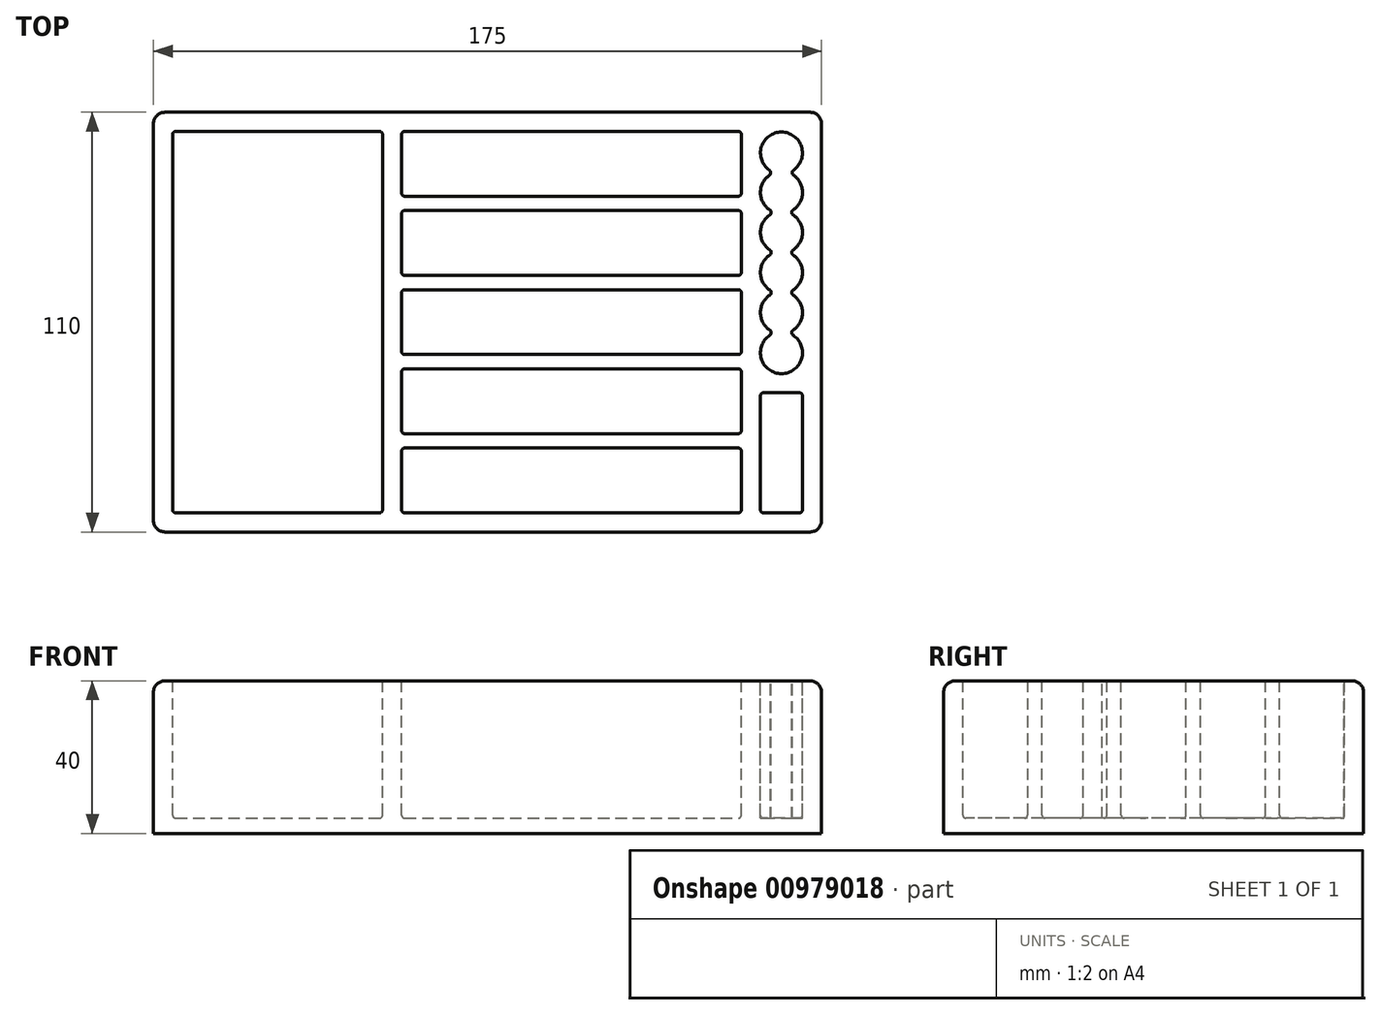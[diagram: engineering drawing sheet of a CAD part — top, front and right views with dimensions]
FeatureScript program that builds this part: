
annotation { "Feature Type Name" : "Feature", "Feature Type Description" : "" }
export const myFeature = defineFeature(function(context is Context, id is Id, definition is map)
    precondition{}
    {
        {
            var Q0;
            Q0=qCreatedBy(makeId("Top.planeOp"),FACE);
            var sketch = newSketch(context, id + "F0", { "sketchPlane" : qUnion([Q0])});
            skLineSegment(sketch, "E0.bottom", {"start": v(87.5, 55) * mm, "end": v(-87.5, 55) * mm});
            skLineSegment(sketch, "E0.top", {"start": v(87.5, -55) * mm, "end": v(-87.5, -55) * mm});
            skLineSegment(sketch, "E0.left", {"start": v(87.5, 55) * mm, "end": v(87.5, -55) * mm});
            skLineSegment(sketch, "E0.right", {"start": v(-87.5, 55) * mm, "end": v(-87.5, -55) * mm});
            skPoint(sketch, "E0.middle", {"position": v(0, 0) * mm});
            skSolve(sketch);
        }
        {
            var Q0;
            Q0=makeQuery(id+"F0.imprint","IMPRINT",FACE,{"disambiguationData":[TD([[makeQuery(id+"F0.imprint","IMPRINT",EDGE,{"derivedFrom":sQuery(id+"F0.wireOp",EDGE,"E0.bottom")}),1.0]])]});
            extrude(context, id + "F1", {"entities" : qUnion([Q0]), "depth" : 40 * mm, "offsetDistance" : 25 * mm});
        }
        {
            var Q0;
            Q0=makeQuery(id+"F1.opExtrude","CAP_FACE",FACE,{"disambiguationData":[OSD([sQuery(id+"F0.wireOp",EDGE,"E0.bottom"),sQuery(id+"F0.wireOp",EDGE,"E0.top"),sQuery(id+"F0.wireOp",EDGE,"E0.left"),sQuery(id+"F0.wireOp",EDGE,"E0.right")])],"isStart":false});
            var sketch = newSketch(context, id + "F2", { "sketchPlane" : qUnion([Q0])});
            skLineSegment(sketch, "E1.bottom", {"start": v(-82.5, 50) * mm, "end": v(-27.5, 50) * mm});
            skLineSegment(sketch, "E1.top", {"start": v(-82.5, -50) * mm, "end": v(-27.5, -50) * mm});
            skLineSegment(sketch, "E1.left", {"start": v(-82.5, 50) * mm, "end": v(-82.5, -50) * mm});
            skLineSegment(sketch, "E1.right", {"start": v(-27.5, 50) * mm, "end": v(-27.5, -50) * mm});
            skLineSegment(sketch, "E2.bottom", {"start": v(-22.5, 50) * mm, "end": v(66.5, 50) * mm});
            skLineSegment(sketch, "E2.top", {"start": v(-22.5, 33) * mm, "end": v(66.5, 33) * mm});
            skLineSegment(sketch, "E2.left", {"start": v(-22.5, 50) * mm, "end": v(-22.5, 33) * mm});
            skLineSegment(sketch, "E2.right", {"start": v(66.5, 50) * mm, "end": v(66.5, 33) * mm});
            skLineSegment(sketch, "E3.bottom", {"start": v(-22.5, 29.25) * mm, "end": v(66.5, 29.25) * mm});
            skLineSegment(sketch, "E3.top", {"start": v(-22.5, 12.25) * mm, "end": v(66.5, 12.25) * mm});
            skLineSegment(sketch, "E3.left", {"start": v(-22.5, 29.25) * mm, "end": v(-22.5, 12.25) * mm});
            skLineSegment(sketch, "E3.right", {"start": v(66.5, 29.25) * mm, "end": v(66.5, 12.25) * mm});
            skCircle(sketch, "E4", {"center": v(77, 34) * mm, "radius": 5.5 * mm});
            skCircle(sketch, "E5", {"center": v(77, 23.5) * mm, "radius": 5.5 * mm});
            skCircle(sketch, "E6", {"center": v(77, 13) * mm, "radius": 5.5 * mm});
            skCircle(sketch, "E7", {"center": v(77, 2.5) * mm, "radius": 5.5 * mm});
            skCircle(sketch, "E8", {"center": v(77, -8) * mm, "radius": 5.5 * mm});
            skPoint(sketch, "E9", {"position": v(77, 44.5) * mm});
            skLineSegment(sketch, "E10.bottom", {"start": v(-22.5, 8.5) * mm, "end": v(66.5, 8.5) * mm});
            skLineSegment(sketch, "E10.top", {"start": v(-22.5, -8.5) * mm, "end": v(66.5, -8.5) * mm});
            skLineSegment(sketch, "E10.left", {"start": v(-22.5, 8.5) * mm, "end": v(-22.5, -8.5) * mm});
            skLineSegment(sketch, "E10.right", {"start": v(66.5, 8.5) * mm, "end": v(66.5, -8.5) * mm});
            skLineSegment(sketch, "E11.bottom", {"start": v(-22.5, -12.25) * mm, "end": v(66.5, -12.25) * mm});
            skLineSegment(sketch, "E11.top", {"start": v(-22.5, -29.25) * mm, "end": v(66.5, -29.25) * mm});
            skLineSegment(sketch, "E11.left", {"start": v(-22.5, -12.25) * mm, "end": v(-22.5, -29.25) * mm});
            skLineSegment(sketch, "E11.right", {"start": v(66.5, -12.25) * mm, "end": v(66.5, -29.25) * mm});
            skLineSegment(sketch, "E12.bottom", {"start": v(-22.5, -33) * mm, "end": v(66.5, -33) * mm});
            skLineSegment(sketch, "E12.top", {"start": v(-22.5, -50) * mm, "end": v(66.5, -50) * mm});
            skLineSegment(sketch, "E12.left", {"start": v(-22.5, -33) * mm, "end": v(-22.5, -50) * mm});
            skLineSegment(sketch, "E12.right", {"start": v(66.5, -33) * mm, "end": v(66.5, -50) * mm});
            skLineSegment(sketch, "E13", {"start": v(-22.5, 50) * mm, "end": v(-22.5, -50) * mm, "construction": true});
            skLineSegment(sketch, "E14", {"start": v(66.5, 50) * mm, "end": v(66.5, -50) * mm, "construction": true});
            skLineSegment(sketch, "E15", {"start": v(77, 46.54) * mm, "end": v(77, -10.4) * mm, "construction": true});
            skLineSegment(sketch, "E16.bottom", {"start": v(71.5, -18.5) * mm, "end": v(82.5, -18.5) * mm});
            skLineSegment(sketch, "E16.top", {"start": v(71.5, -50) * mm, "end": v(82.5, -50) * mm});
            skLineSegment(sketch, "E16.left", {"start": v(71.5, -18.5) * mm, "end": v(71.5, -50) * mm});
            skLineSegment(sketch, "E16.right", {"start": v(82.5, -18.5) * mm, "end": v(82.5, -50) * mm});
            skPoint(sketch, "E17", {"position": v(77, 52.56) * mm});
            skCircle(sketch, "E18", {"center": v(77, 44.33) * mm, "radius": 5.5 * mm});
            skSolve(sketch);
        }
        {
            var Q0;
            {var subQ0=sQuery(id+"F2.wireOp",EDGE,"E4");var subQ1=sQuery(id+"F2.wireOp",EDGE,"6KCrKnpJ-FuMg-xrRx-nZZj-uacWkpcAq4VA");var subQ2=makeQuery(id+"F2.imprint","INTERSECT",VERTEX,{"disambiguationData":[OD(0.0)],"derivedFrom":[subQ1,subQ0]});Q0=makeQuery(id+"F2.imprint","IMPRINT",FACE,{"disambiguationData":[TD([[makeQuery(id+"F2.imprint","IMPRINT",EDGE,{"disambiguationData":[TD([[subQ2,1.0]])],"derivedFrom":subQ1}),1.0]])]});}
            var Q1;
            {var subQ0=sQuery(id+"F2.wireOp",EDGE,"E4");var subQ1=sQuery(id+"F2.wireOp",EDGE,"6KCrKnpJ-FuMg-xrRx-nZZj-uacWkpcAq4VA");var subQ2=makeQuery(id+"F2.imprint","INTERSECT",VERTEX,{"disambiguationData":[OD(0.0)],"derivedFrom":[subQ1,subQ0]});Q1=makeQuery(id+"F2.imprint","IMPRINT",FACE,{"disambiguationData":[TD([[makeQuery(id+"F2.imprint","IMPRINT",EDGE,{"disambiguationData":[TD([[subQ2,-1.0]])],"derivedFrom":subQ1}),1.0]])]});}
            var Q2;
            {var subQ0=sQuery(id+"F2.wireOp",EDGE,"E5");var subQ1=sQuery(id+"F2.wireOp",EDGE,"E4");var subQ2=makeQuery(id+"F2.imprint","INTERSECT",VERTEX,{"disambiguationData":[OD(0.0)],"derivedFrom":[subQ1,subQ0]});Q2=makeQuery(id+"F2.imprint","IMPRINT",FACE,{"disambiguationData":[TD([[makeQuery(id+"F2.imprint","IMPRINT",EDGE,{"disambiguationData":[TD([[subQ2,-1.0]])],"derivedFrom":subQ1}),1.0]])]});}
            var Q3;
            {var subQ0=sQuery(id+"F2.wireOp",EDGE,"E5");var subQ1=sQuery(id+"F2.wireOp",EDGE,"E4");var subQ2=makeQuery(id+"F2.imprint","INTERSECT",VERTEX,{"disambiguationData":[OD(0.0)],"derivedFrom":[subQ1,subQ0]});Q3=makeQuery(id+"F2.imprint","IMPRINT",FACE,{"disambiguationData":[TD([[makeQuery(id+"F2.imprint","IMPRINT",EDGE,{"disambiguationData":[TD([[subQ2,-1.0]])],"derivedFrom":subQ1}),-1.0]])]});}
            var Q4;
            {var subQ0=sQuery(id+"F2.wireOp",EDGE,"E6");var subQ1=sQuery(id+"F2.wireOp",EDGE,"E5");var subQ2=makeQuery(id+"F2.imprint","INTERSECT",VERTEX,{"disambiguationData":[OD(0.0)],"derivedFrom":[subQ1,subQ0]});Q4=makeQuery(id+"F2.imprint","IMPRINT",FACE,{"disambiguationData":[TD([[makeQuery(id+"F2.imprint","IMPRINT",EDGE,{"disambiguationData":[TD([[subQ2,-1.0]])],"derivedFrom":subQ1}),1.0]])]});}
            var Q5;
            {var subQ0=sQuery(id+"F2.wireOp",EDGE,"E6");var subQ1=sQuery(id+"F2.wireOp",EDGE,"E5");var subQ2=makeQuery(id+"F2.imprint","INTERSECT",VERTEX,{"disambiguationData":[OD(0.0)],"derivedFrom":[subQ1,subQ0]});Q5=makeQuery(id+"F2.imprint","IMPRINT",FACE,{"disambiguationData":[TD([[makeQuery(id+"F2.imprint","IMPRINT",EDGE,{"disambiguationData":[TD([[subQ2,-1.0]])],"derivedFrom":subQ1}),-1.0]])]});}
            var Q6;
            {var subQ0=sQuery(id+"F2.wireOp",EDGE,"E7");var subQ1=sQuery(id+"F2.wireOp",EDGE,"E6");var subQ2=makeQuery(id+"F2.imprint","INTERSECT",VERTEX,{"disambiguationData":[OD(0.0)],"derivedFrom":[subQ1,subQ0]});Q6=makeQuery(id+"F2.imprint","IMPRINT",FACE,{"disambiguationData":[TD([[makeQuery(id+"F2.imprint","IMPRINT",EDGE,{"disambiguationData":[TD([[subQ2,-1.0]])],"derivedFrom":subQ1}),-1.0]])]});}
            var Q7;
            {var subQ0=sQuery(id+"F2.wireOp",EDGE,"E7");var subQ1=sQuery(id+"F2.wireOp",EDGE,"E6");var subQ2=makeQuery(id+"F2.imprint","INTERSECT",VERTEX,{"disambiguationData":[OD(0.0)],"derivedFrom":[subQ1,subQ0]});Q7=makeQuery(id+"F2.imprint","IMPRINT",FACE,{"disambiguationData":[TD([[makeQuery(id+"F2.imprint","IMPRINT",EDGE,{"disambiguationData":[TD([[subQ2,-1.0]])],"derivedFrom":subQ1}),1.0]])]});}
            var Q8;
            {var subQ0=sQuery(id+"F2.wireOp",EDGE,"E8");var subQ1=sQuery(id+"F2.wireOp",EDGE,"E7");var subQ2=makeQuery(id+"F2.imprint","INTERSECT",VERTEX,{"disambiguationData":[OD(0.0)],"derivedFrom":[subQ1,subQ0]});Q8=makeQuery(id+"F2.imprint","IMPRINT",FACE,{"disambiguationData":[TD([[makeQuery(id+"F2.imprint","IMPRINT",EDGE,{"disambiguationData":[TD([[subQ2,-1.0]])],"derivedFrom":subQ1}),1.0]])]});}
            var Q9;
            {var subQ0=sQuery(id+"F2.wireOp",EDGE,"E8");var subQ1=sQuery(id+"F2.wireOp",EDGE,"E7");var subQ2=makeQuery(id+"F2.imprint","INTERSECT",VERTEX,{"disambiguationData":[OD(0.0)],"derivedFrom":[subQ1,subQ0]});Q9=makeQuery(id+"F2.imprint","IMPRINT",FACE,{"disambiguationData":[TD([[makeQuery(id+"F2.imprint","IMPRINT",EDGE,{"disambiguationData":[TD([[subQ2,-1.0]])],"derivedFrom":subQ1}),-1.0]])]});}
            var Q10;
            {var subQ0=sQuery(id+"F2.wireOp",EDGE,"E4");var subQ1=sQuery(id+"F2.wireOp",EDGE,"6KCrKnpJ-FuMg-xrRx-nZZj-uacWkpcAq4VA");var subQ2=makeQuery(id+"F2.imprint","INTERSECT",VERTEX,{"disambiguationData":[OD(0.0)],"derivedFrom":[subQ1,subQ0]});Q10=makeQuery(id+"F2.imprint","IMPRINT",FACE,{"disambiguationData":[TD([[makeQuery(id+"F2.imprint","IMPRINT",EDGE,{"disambiguationData":[TD([[subQ2,-1.0]])],"derivedFrom":subQ1}),-1.0]])]});}
            var Q11;
            Q11=makeQuery(id+"F2.imprint","IMPRINT",FACE,{"disambiguationData":[TD([[makeQuery(id+"F2.imprint","IMPRINT",EDGE,{"derivedFrom":sQuery(id+"F2.wireOp",EDGE,"E1.bottom")}),-1.0]])]});
            var Q12;
            Q12=makeQuery(id+"F2.imprint","IMPRINT",FACE,{"disambiguationData":[TD([[makeQuery(id+"F2.imprint","IMPRINT",EDGE,{"derivedFrom":sQuery(id+"F2.wireOp",EDGE,"E2.bottom")}),-1.0]])]});
            var Q13;
            Q13=makeQuery(id+"F2.imprint","IMPRINT",FACE,{"disambiguationData":[TD([[makeQuery(id+"F2.imprint","IMPRINT",EDGE,{"derivedFrom":sQuery(id+"F2.wireOp",EDGE,"E3.bottom")}),-1.0]])]});
            var Q14;
            Q14=makeQuery(id+"F2.imprint","IMPRINT",FACE,{"disambiguationData":[TD([[makeQuery(id+"F2.imprint","IMPRINT",EDGE,{"derivedFrom":sQuery(id+"F2.wireOp",EDGE,"E10.bottom")}),-1.0]])]});
            var Q15;
            Q15=makeQuery(id+"F2.imprint","IMPRINT",FACE,{"disambiguationData":[TD([[makeQuery(id+"F2.imprint","IMPRINT",EDGE,{"derivedFrom":sQuery(id+"F2.wireOp",EDGE,"E11.bottom")}),-1.0]])]});
            var Q16;
            Q16=makeQuery(id+"F2.imprint","IMPRINT",FACE,{"disambiguationData":[TD([[makeQuery(id+"F2.imprint","IMPRINT",EDGE,{"derivedFrom":sQuery(id+"F2.wireOp",EDGE,"E12.bottom")}),-1.0]])]});
            var Q17;
            Q17=makeQuery(id+"F2.imprint","IMPRINT",FACE,{"disambiguationData":[TD([[makeQuery(id+"F2.imprint","IMPRINT",EDGE,{"derivedFrom":sQuery(id+"F2.wireOp",EDGE,"E16.bottom")}),-1.0]])]});
            var Q18;
            {var subQ0=sQuery(id+"F2.wireOp",EDGE,"E18");var subQ1=sQuery(id+"F2.wireOp",EDGE,"E4");var subQ2=makeQuery(id+"F2.imprint","INTERSECT",VERTEX,{"disambiguationData":[OD(0.0)],"derivedFrom":[subQ1,subQ0]});Q18=makeQuery(id+"F2.imprint","IMPRINT",FACE,{"disambiguationData":[TD([[makeQuery(id+"F2.imprint","IMPRINT",EDGE,{"disambiguationData":[TD([[subQ2,-1.0]])],"derivedFrom":subQ1}),1.0]])]});}
            var Q19;
            {var subQ0=sQuery(id+"F2.wireOp",EDGE,"E18");var subQ1=sQuery(id+"F2.wireOp",EDGE,"E4");var subQ2=makeQuery(id+"F2.imprint","INTERSECT",VERTEX,{"disambiguationData":[OD(0.0)],"derivedFrom":[subQ1,subQ0]});Q19=makeQuery(id+"F2.imprint","IMPRINT",FACE,{"disambiguationData":[TD([[makeQuery(id+"F2.imprint","IMPRINT",EDGE,{"disambiguationData":[TD([[subQ2,1.0]])],"derivedFrom":subQ1}),1.0]])]});}
            var Q20;
            {var subQ0=sQuery(id+"F2.wireOp",EDGE,"E18");var subQ1=sQuery(id+"F2.wireOp",EDGE,"E4");var subQ2=makeQuery(id+"F2.imprint","INTERSECT",VERTEX,{"disambiguationData":[OD(0.0)],"derivedFrom":[subQ1,subQ0]});Q20=makeQuery(id+"F2.imprint","IMPRINT",FACE,{"disambiguationData":[TD([[makeQuery(id+"F2.imprint","IMPRINT",EDGE,{"disambiguationData":[TD([[subQ2,1.0]])],"derivedFrom":subQ1}),-1.0]])]});}
            extrude(context, id + "F3", {"entities" : qUnion([Q0, Q1, Q2, Q3, Q4, Q5, Q6, Q7, Q8, Q9, Q10, Q11, Q12, Q13, Q14, Q15, Q16, Q17, Q18, Q19, Q20]), "operationType" : NewBodyOperationType.REMOVE, "oppositeDirection" : true, "depth" : 36 * mm, "offsetDistance" : 25 * mm});
        }
        {
            var Q0;
            {var subQ0=sQuery(id+"F2.wireOp",EDGE,"E4");var subQ1=sQuery(id+"F2.wireOp",EDGE,"6KCrKnpJ-FuMg-xrRx-nZZj-uacWkpcAq4VA");Q0=makeQuery(id+"F3.boolean.opBoolean","COPY",EDGE,{"derivedFrom":makeQuery(id+"F3.opExtrude","SWEPT_EDGE",EDGE,{"disambiguationData":[OSD([subQ1,subQ0]),TDD([makeQuery(id+"F2.imprint","INTERSECT",VERTEX,{"disambiguationData":[OD(0.0)],"derivedFrom":[subQ1,subQ0]})])]})});}
            var Q1;
            {var subQ0=sQuery(id+"F2.wireOp",EDGE,"E5");var subQ1=sQuery(id+"F2.wireOp",EDGE,"E4");Q1=makeQuery(id+"F3.boolean.opBoolean","COPY",EDGE,{"derivedFrom":makeQuery(id+"F3.opExtrude","SWEPT_EDGE",EDGE,{"disambiguationData":[OSD([subQ1,subQ0]),TDD([makeQuery(id+"F2.imprint","INTERSECT",VERTEX,{"disambiguationData":[OD(0.0)],"derivedFrom":[subQ1,subQ0]})])]})});}
            var Q2;
            {var subQ0=sQuery(id+"F2.wireOp",EDGE,"E6");var subQ1=sQuery(id+"F2.wireOp",EDGE,"E5");Q2=makeQuery(id+"F3.boolean.opBoolean","COPY",EDGE,{"derivedFrom":makeQuery(id+"F3.opExtrude","SWEPT_EDGE",EDGE,{"disambiguationData":[OSD([subQ1,subQ0]),TDD([makeQuery(id+"F2.imprint","INTERSECT",VERTEX,{"disambiguationData":[OD(0.0)],"derivedFrom":[subQ1,subQ0]})])]})});}
            var Q3;
            {var subQ0=sQuery(id+"F2.wireOp",EDGE,"E7");var subQ1=sQuery(id+"F2.wireOp",EDGE,"E6");Q3=makeQuery(id+"F3.boolean.opBoolean","COPY",EDGE,{"derivedFrom":makeQuery(id+"F3.opExtrude","SWEPT_EDGE",EDGE,{"disambiguationData":[OSD([subQ1,subQ0]),TDD([makeQuery(id+"F2.imprint","INTERSECT",VERTEX,{"disambiguationData":[OD(0.0)],"derivedFrom":[subQ1,subQ0]})])]})});}
            var Q4;
            {var subQ0=sQuery(id+"F2.wireOp",EDGE,"E8");var subQ1=sQuery(id+"F2.wireOp",EDGE,"E7");Q4=makeQuery(id+"F3.boolean.opBoolean","COPY",EDGE,{"derivedFrom":makeQuery(id+"F3.opExtrude","SWEPT_EDGE",EDGE,{"disambiguationData":[OSD([subQ1,subQ0]),TDD([makeQuery(id+"F2.imprint","INTERSECT",VERTEX,{"disambiguationData":[OD(0.0)],"derivedFrom":[subQ1,subQ0]})])]})});}
            var Q5;
            {var subQ0=sQuery(id+"F2.wireOp",EDGE,"E8");var subQ1=sQuery(id+"F2.wireOp",EDGE,"E7");Q5=makeQuery(id+"F3.boolean.opBoolean","COPY",EDGE,{"derivedFrom":makeQuery(id+"F3.opExtrude","SWEPT_EDGE",EDGE,{"disambiguationData":[OSD([subQ1,subQ0]),TDD([makeQuery(id+"F2.imprint","INTERSECT",VERTEX,{"disambiguationData":[OD(1.0)],"derivedFrom":[subQ1,subQ0]})])]})});}
            var Q6;
            {var subQ0=sQuery(id+"F2.wireOp",EDGE,"E7");var subQ1=sQuery(id+"F2.wireOp",EDGE,"E6");Q6=makeQuery(id+"F3.boolean.opBoolean","COPY",EDGE,{"derivedFrom":makeQuery(id+"F3.opExtrude","SWEPT_EDGE",EDGE,{"disambiguationData":[OSD([subQ1,subQ0]),TDD([makeQuery(id+"F2.imprint","INTERSECT",VERTEX,{"disambiguationData":[OD(1.0)],"derivedFrom":[subQ1,subQ0]})])]})});}
            var Q7;
            {var subQ0=sQuery(id+"F2.wireOp",EDGE,"E6");var subQ1=sQuery(id+"F2.wireOp",EDGE,"E5");Q7=makeQuery(id+"F3.boolean.opBoolean","COPY",EDGE,{"derivedFrom":makeQuery(id+"F3.opExtrude","SWEPT_EDGE",EDGE,{"disambiguationData":[OSD([subQ1,subQ0]),TDD([makeQuery(id+"F2.imprint","INTERSECT",VERTEX,{"disambiguationData":[OD(1.0)],"derivedFrom":[subQ1,subQ0]})])]})});}
            var Q8;
            {var subQ0=sQuery(id+"F2.wireOp",EDGE,"E5");var subQ1=sQuery(id+"F2.wireOp",EDGE,"E4");Q8=makeQuery(id+"F3.boolean.opBoolean","COPY",EDGE,{"derivedFrom":makeQuery(id+"F3.opExtrude","SWEPT_EDGE",EDGE,{"disambiguationData":[OSD([subQ1,subQ0]),TDD([makeQuery(id+"F2.imprint","INTERSECT",VERTEX,{"disambiguationData":[OD(1.0)],"derivedFrom":[subQ1,subQ0]})])]})});}
            var Q9;
            {var subQ0=sQuery(id+"F2.wireOp",EDGE,"E4");var subQ1=sQuery(id+"F2.wireOp",EDGE,"6KCrKnpJ-FuMg-xrRx-nZZj-uacWkpcAq4VA");Q9=makeQuery(id+"F3.boolean.opBoolean","COPY",EDGE,{"derivedFrom":makeQuery(id+"F3.opExtrude","SWEPT_EDGE",EDGE,{"disambiguationData":[OSD([subQ1,subQ0]),TDD([makeQuery(id+"F2.imprint","INTERSECT",VERTEX,{"disambiguationData":[OD(1.0)],"derivedFrom":[subQ1,subQ0]})])]})});}
            var Q10;
            Q10=makeQuery(id+"F3.boolean.opBoolean","COPY",EDGE,{"derivedFrom":makeQuery(id+"F3.opExtrude","SWEPT_EDGE",EDGE,{"disambiguationData":[OSD([sQuery(id+"F2.wireOp",EDGE,"E2.bottom"),sQuery(id+"F2.wireOp",EDGE,"E2.right")])]})});
            var Q11;
            Q11=makeQuery(id+"F3.boolean.opBoolean","COPY",EDGE,{"derivedFrom":makeQuery(id+"F3.opExtrude","CAP_EDGE",EDGE,{"disambiguationData":[OSD([sQuery(id+"F2.wireOp",EDGE,"E2.bottom")])],"isStart":false})});
            var Q12;
            Q12=makeQuery(id+"F3.boolean.opBoolean","COPY",EDGE,{"derivedFrom":makeQuery(id+"F3.opExtrude","CAP_EDGE",EDGE,{"disambiguationData":[OSD([sQuery(id+"F2.wireOp",EDGE,"E2.right")])],"isStart":false})});
            var Q13;
            Q13=makeQuery(id+"F3.boolean.opBoolean","COPY",EDGE,{"derivedFrom":makeQuery(id+"F3.opExtrude","CAP_EDGE",EDGE,{"disambiguationData":[OSD([sQuery(id+"F2.wireOp",EDGE,"E2.top")])],"isStart":false})});
            var Q14;
            Q14=makeQuery(id+"F3.boolean.opBoolean","COPY",EDGE,{"derivedFrom":makeQuery(id+"F3.opExtrude","CAP_EDGE",EDGE,{"disambiguationData":[OSD([sQuery(id+"F2.wireOp",EDGE,"E2.left")])],"isStart":false})});
            var Q15;
            Q15=makeQuery(id+"F3.boolean.opBoolean","COPY",EDGE,{"derivedFrom":makeQuery(id+"F3.opExtrude","SWEPT_EDGE",EDGE,{"disambiguationData":[OSD([sQuery(id+"F2.wireOp",EDGE,"E2.bottom"),sQuery(id+"F2.wireOp",EDGE,"E2.left")])]})});
            var Q16;
            Q16=makeQuery(id+"F3.boolean.opBoolean","COPY",EDGE,{"derivedFrom":makeQuery(id+"F3.opExtrude","SWEPT_EDGE",EDGE,{"disambiguationData":[OSD([sQuery(id+"F2.wireOp",EDGE,"E2.top"),sQuery(id+"F2.wireOp",EDGE,"E2.left")])]})});
            var Q17;
            Q17=makeQuery(id+"F3.boolean.opBoolean","COPY",EDGE,{"derivedFrom":makeQuery(id+"F3.opExtrude","SWEPT_EDGE",EDGE,{"disambiguationData":[OSD([sQuery(id+"F2.wireOp",EDGE,"E2.top"),sQuery(id+"F2.wireOp",EDGE,"E2.right")])]})});
            var Q18;
            Q18=makeQuery(id+"F3.boolean.opBoolean","COPY",EDGE,{"derivedFrom":makeQuery(id+"F3.opExtrude","SWEPT_EDGE",EDGE,{"disambiguationData":[OSD([sQuery(id+"F2.wireOp",EDGE,"E3.bottom"),sQuery(id+"F2.wireOp",EDGE,"E3.right")])]})});
            var Q19;
            Q19=makeQuery(id+"F3.boolean.opBoolean","COPY",EDGE,{"derivedFrom":makeQuery(id+"F3.opExtrude","CAP_EDGE",EDGE,{"disambiguationData":[OSD([sQuery(id+"F2.wireOp",EDGE,"E3.bottom")])],"isStart":false})});
            var Q20;
            Q20=makeQuery(id+"F3.boolean.opBoolean","COPY",EDGE,{"derivedFrom":makeQuery(id+"F3.opExtrude","CAP_EDGE",EDGE,{"disambiguationData":[OSD([sQuery(id+"F2.wireOp",EDGE,"E3.right")])],"isStart":false})});
            var Q21;
            Q21=makeQuery(id+"F3.boolean.opBoolean","COPY",EDGE,{"derivedFrom":makeQuery(id+"F3.opExtrude","CAP_EDGE",EDGE,{"disambiguationData":[OSD([sQuery(id+"F2.wireOp",EDGE,"E3.top")])],"isStart":false})});
            var Q22;
            Q22=makeQuery(id+"F3.boolean.opBoolean","COPY",EDGE,{"derivedFrom":makeQuery(id+"F3.opExtrude","SWEPT_EDGE",EDGE,{"disambiguationData":[OSD([sQuery(id+"F2.wireOp",EDGE,"E3.top"),sQuery(id+"F2.wireOp",EDGE,"E3.right")])]})});
            var Q23;
            Q23=makeQuery(id+"F3.boolean.opBoolean","COPY",EDGE,{"derivedFrom":makeQuery(id+"F3.opExtrude","SWEPT_EDGE",EDGE,{"disambiguationData":[OSD([sQuery(id+"F2.wireOp",EDGE,"E3.bottom"),sQuery(id+"F2.wireOp",EDGE,"E3.left")])]})});
            var Q24;
            Q24=makeQuery(id+"F3.boolean.opBoolean","COPY",EDGE,{"derivedFrom":makeQuery(id+"F3.opExtrude","CAP_EDGE",EDGE,{"disambiguationData":[OSD([sQuery(id+"F2.wireOp",EDGE,"E3.left")])],"isStart":false})});
            var Q25;
            Q25=makeQuery(id+"F3.boolean.opBoolean","COPY",EDGE,{"derivedFrom":makeQuery(id+"F3.opExtrude","SWEPT_EDGE",EDGE,{"disambiguationData":[OSD([sQuery(id+"F2.wireOp",EDGE,"E3.top"),sQuery(id+"F2.wireOp",EDGE,"E3.left")])]})});
            var Q26;
            Q26=makeQuery(id+"F3.boolean.opBoolean","COPY",EDGE,{"derivedFrom":makeQuery(id+"F3.opExtrude","SWEPT_EDGE",EDGE,{"disambiguationData":[OSD([sQuery(id+"F2.wireOp",EDGE,"E10.bottom"),sQuery(id+"F2.wireOp",EDGE,"E10.right")])]})});
            var Q27;
            Q27=makeQuery(id+"F3.boolean.opBoolean","COPY",EDGE,{"derivedFrom":makeQuery(id+"F3.opExtrude","CAP_EDGE",EDGE,{"disambiguationData":[OSD([sQuery(id+"F2.wireOp",EDGE,"E10.bottom")])],"isStart":false})});
            var Q28;
            Q28=makeQuery(id+"F3.boolean.opBoolean","COPY",EDGE,{"derivedFrom":makeQuery(id+"F3.opExtrude","CAP_EDGE",EDGE,{"disambiguationData":[OSD([sQuery(id+"F2.wireOp",EDGE,"E10.right")])],"isStart":false})});
            var Q29;
            Q29=makeQuery(id+"F3.boolean.opBoolean","COPY",EDGE,{"derivedFrom":makeQuery(id+"F3.opExtrude","CAP_EDGE",EDGE,{"disambiguationData":[OSD([sQuery(id+"F2.wireOp",EDGE,"E10.top")])],"isStart":false})});
            var Q30;
            Q30=makeQuery(id+"F3.boolean.opBoolean","COPY",EDGE,{"derivedFrom":makeQuery(id+"F3.opExtrude","SWEPT_EDGE",EDGE,{"disambiguationData":[OSD([sQuery(id+"F2.wireOp",EDGE,"E10.top"),sQuery(id+"F2.wireOp",EDGE,"E10.right")])]})});
            var Q31;
            Q31=makeQuery(id+"F3.boolean.opBoolean","COPY",EDGE,{"derivedFrom":makeQuery(id+"F3.opExtrude","SWEPT_EDGE",EDGE,{"disambiguationData":[OSD([sQuery(id+"F2.wireOp",EDGE,"E10.top"),sQuery(id+"F2.wireOp",EDGE,"E10.left")])]})});
            var Q32;
            Q32=makeQuery(id+"F3.boolean.opBoolean","COPY",EDGE,{"derivedFrom":makeQuery(id+"F3.opExtrude","SWEPT_EDGE",EDGE,{"disambiguationData":[OSD([sQuery(id+"F2.wireOp",EDGE,"E10.bottom"),sQuery(id+"F2.wireOp",EDGE,"E10.left")])]})});
            var Q33;
            Q33=makeQuery(id+"F3.boolean.opBoolean","COPY",EDGE,{"derivedFrom":makeQuery(id+"F3.opExtrude","CAP_EDGE",EDGE,{"disambiguationData":[OSD([sQuery(id+"F2.wireOp",EDGE,"E10.left")])],"isStart":false})});
            var Q34;
            Q34=makeQuery(id+"F3.boolean.opBoolean","COPY",EDGE,{"derivedFrom":makeQuery(id+"F3.opExtrude","SWEPT_EDGE",EDGE,{"disambiguationData":[OSD([sQuery(id+"F2.wireOp",EDGE,"E11.bottom"),sQuery(id+"F2.wireOp",EDGE,"E11.right")])]})});
            var Q35;
            Q35=makeQuery(id+"F3.boolean.opBoolean","COPY",EDGE,{"derivedFrom":makeQuery(id+"F3.opExtrude","SWEPT_EDGE",EDGE,{"disambiguationData":[OSD([sQuery(id+"F2.wireOp",EDGE,"E11.top"),sQuery(id+"F2.wireOp",EDGE,"E11.right")])]})});
            var Q36;
            Q36=makeQuery(id+"F3.boolean.opBoolean","COPY",EDGE,{"derivedFrom":makeQuery(id+"F3.opExtrude","CAP_EDGE",EDGE,{"disambiguationData":[OSD([sQuery(id+"F2.wireOp",EDGE,"E11.right")])],"isStart":false})});
            var Q37;
            Q37=makeQuery(id+"F3.boolean.opBoolean","COPY",EDGE,{"derivedFrom":makeQuery(id+"F3.opExtrude","CAP_EDGE",EDGE,{"disambiguationData":[OSD([sQuery(id+"F2.wireOp",EDGE,"E11.top")])],"isStart":false})});
            var Q38;
            Q38=makeQuery(id+"F3.boolean.opBoolean","COPY",EDGE,{"derivedFrom":makeQuery(id+"F3.opExtrude","CAP_EDGE",EDGE,{"disambiguationData":[OSD([sQuery(id+"F2.wireOp",EDGE,"E11.bottom")])],"isStart":false})});
            var Q39;
            Q39=makeQuery(id+"F3.boolean.opBoolean","COPY",EDGE,{"derivedFrom":makeQuery(id+"F3.opExtrude","SWEPT_EDGE",EDGE,{"disambiguationData":[OSD([sQuery(id+"F2.wireOp",EDGE,"E11.bottom"),sQuery(id+"F2.wireOp",EDGE,"E11.left")])]})});
            var Q40;
            Q40=makeQuery(id+"F3.boolean.opBoolean","COPY",EDGE,{"derivedFrom":makeQuery(id+"F3.opExtrude","CAP_EDGE",EDGE,{"disambiguationData":[OSD([sQuery(id+"F2.wireOp",EDGE,"E11.left")])],"isStart":false})});
            var Q41;
            Q41=makeQuery(id+"F3.boolean.opBoolean","COPY",EDGE,{"derivedFrom":makeQuery(id+"F3.opExtrude","SWEPT_EDGE",EDGE,{"disambiguationData":[OSD([sQuery(id+"F2.wireOp",EDGE,"E11.top"),sQuery(id+"F2.wireOp",EDGE,"E11.left")])]})});
            var Q42;
            Q42=makeQuery(id+"F3.boolean.opBoolean","COPY",EDGE,{"derivedFrom":makeQuery(id+"F3.opExtrude","SWEPT_EDGE",EDGE,{"disambiguationData":[OSD([sQuery(id+"F2.wireOp",EDGE,"E12.top"),sQuery(id+"F2.wireOp",EDGE,"E12.left")])]})});
            var Q43;
            Q43=makeQuery(id+"F3.boolean.opBoolean","COPY",EDGE,{"derivedFrom":makeQuery(id+"F3.opExtrude","CAP_EDGE",EDGE,{"disambiguationData":[OSD([sQuery(id+"F2.wireOp",EDGE,"E12.top")])],"isStart":false})});
            var Q44;
            Q44=makeQuery(id+"F3.boolean.opBoolean","COPY",EDGE,{"derivedFrom":makeQuery(id+"F3.opExtrude","CAP_EDGE",EDGE,{"disambiguationData":[OSD([sQuery(id+"F2.wireOp",EDGE,"E12.left")])],"isStart":false})});
            var Q45;
            Q45=makeQuery(id+"F3.boolean.opBoolean","COPY",EDGE,{"derivedFrom":makeQuery(id+"F3.opExtrude","SWEPT_EDGE",EDGE,{"disambiguationData":[OSD([sQuery(id+"F2.wireOp",EDGE,"E12.bottom"),sQuery(id+"F2.wireOp",EDGE,"E12.left")])]})});
            var Q46;
            Q46=makeQuery(id+"F3.boolean.opBoolean","COPY",EDGE,{"derivedFrom":makeQuery(id+"F3.opExtrude","CAP_EDGE",EDGE,{"disambiguationData":[OSD([sQuery(id+"F2.wireOp",EDGE,"E12.bottom")])],"isStart":false})});
            var Q47;
            Q47=makeQuery(id+"F3.boolean.opBoolean","COPY",EDGE,{"derivedFrom":makeQuery(id+"F3.opExtrude","SWEPT_EDGE",EDGE,{"disambiguationData":[OSD([sQuery(id+"F2.wireOp",EDGE,"E12.bottom"),sQuery(id+"F2.wireOp",EDGE,"E12.right")])]})});
            var Q48;
            Q48=makeQuery(id+"F3.boolean.opBoolean","COPY",EDGE,{"derivedFrom":makeQuery(id+"F3.opExtrude","CAP_EDGE",EDGE,{"disambiguationData":[OSD([sQuery(id+"F2.wireOp",EDGE,"E12.right")])],"isStart":false})});
            var Q49;
            Q49=makeQuery(id+"F3.boolean.opBoolean","COPY",EDGE,{"derivedFrom":makeQuery(id+"F3.opExtrude","SWEPT_EDGE",EDGE,{"disambiguationData":[OSD([sQuery(id+"F2.wireOp",EDGE,"E12.top"),sQuery(id+"F2.wireOp",EDGE,"E12.right")])]})});
            var Q50;
            Q50=makeQuery(id+"F3.boolean.opBoolean","COPY",EDGE,{"derivedFrom":makeQuery(id+"F3.opExtrude","CAP_EDGE",EDGE,{"disambiguationData":[OSD([sQuery(id+"F2.wireOp",EDGE,"E1.right")])],"isStart":false})});
            var Q51;
            Q51=makeQuery(id+"F3.boolean.opBoolean","COPY",EDGE,{"derivedFrom":makeQuery(id+"F3.opExtrude","SWEPT_EDGE",EDGE,{"disambiguationData":[OSD([sQuery(id+"F2.wireOp",EDGE,"E1.top"),sQuery(id+"F2.wireOp",EDGE,"E1.right")])]})});
            var Q52;
            Q52=makeQuery(id+"F3.boolean.opBoolean","COPY",EDGE,{"derivedFrom":makeQuery(id+"F3.opExtrude","CAP_EDGE",EDGE,{"disambiguationData":[OSD([sQuery(id+"F2.wireOp",EDGE,"E1.top")])],"isStart":false})});
            var Q53;
            Q53=makeQuery(id+"F3.boolean.opBoolean","COPY",EDGE,{"derivedFrom":makeQuery(id+"F3.opExtrude","SWEPT_EDGE",EDGE,{"disambiguationData":[OSD([sQuery(id+"F2.wireOp",EDGE,"E1.bottom"),sQuery(id+"F2.wireOp",EDGE,"E1.right")])]})});
            var Q54;
            Q54=makeQuery(id+"F3.boolean.opBoolean","COPY",EDGE,{"derivedFrom":makeQuery(id+"F3.opExtrude","CAP_EDGE",EDGE,{"disambiguationData":[OSD([sQuery(id+"F2.wireOp",EDGE,"E1.bottom")])],"isStart":false})});
            var Q55;
            Q55=makeQuery(id+"F3.boolean.opBoolean","COPY",EDGE,{"derivedFrom":makeQuery(id+"F3.opExtrude","SWEPT_EDGE",EDGE,{"disambiguationData":[OSD([sQuery(id+"F2.wireOp",EDGE,"E1.bottom"),sQuery(id+"F2.wireOp",EDGE,"E1.left")])]})});
            var Q56;
            Q56=makeQuery(id+"F3.boolean.opBoolean","COPY",EDGE,{"derivedFrom":makeQuery(id+"F3.opExtrude","CAP_EDGE",EDGE,{"disambiguationData":[OSD([sQuery(id+"F2.wireOp",EDGE,"E1.left")])],"isStart":false})});
            var Q57;
            Q57=makeQuery(id+"F3.boolean.opBoolean","COPY",EDGE,{"derivedFrom":makeQuery(id+"F3.opExtrude","SWEPT_EDGE",EDGE,{"disambiguationData":[OSD([sQuery(id+"F2.wireOp",EDGE,"E1.top"),sQuery(id+"F2.wireOp",EDGE,"E1.left")])]})});
            var Q58;
            Q58=makeQuery(id+"F3.boolean.opBoolean","COPY",EDGE,{"derivedFrom":makeQuery(id+"F3.opExtrude","SWEPT_EDGE",EDGE,{"disambiguationData":[OSD([sQuery(id+"F2.wireOp",EDGE,"E16.bottom"),sQuery(id+"F2.wireOp",EDGE,"E16.left")])]})});
            var Q59;
            Q59=makeQuery(id+"F3.boolean.opBoolean","COPY",EDGE,{"derivedFrom":makeQuery(id+"F3.opExtrude","CAP_EDGE",EDGE,{"disambiguationData":[OSD([sQuery(id+"F2.wireOp",EDGE,"E16.bottom")])],"isStart":false})});
            var Q60;
            Q60=makeQuery(id+"F3.boolean.opBoolean","COPY",EDGE,{"derivedFrom":makeQuery(id+"F3.opExtrude","CAP_EDGE",EDGE,{"disambiguationData":[OSD([sQuery(id+"F2.wireOp",EDGE,"E16.left")])],"isStart":false})});
            var Q61;
            Q61=makeQuery(id+"F3.boolean.opBoolean","COPY",EDGE,{"derivedFrom":makeQuery(id+"F3.opExtrude","SWEPT_EDGE",EDGE,{"disambiguationData":[OSD([sQuery(id+"F2.wireOp",EDGE,"E16.top"),sQuery(id+"F2.wireOp",EDGE,"E16.left")])]})});
            var Q62;
            Q62=makeQuery(id+"F3.boolean.opBoolean","COPY",EDGE,{"derivedFrom":makeQuery(id+"F3.opExtrude","CAP_EDGE",EDGE,{"disambiguationData":[OSD([sQuery(id+"F2.wireOp",EDGE,"E16.top")])],"isStart":false})});
            var Q63;
            Q63=makeQuery(id+"F3.boolean.opBoolean","COPY",EDGE,{"derivedFrom":makeQuery(id+"F3.opExtrude","SWEPT_EDGE",EDGE,{"disambiguationData":[OSD([sQuery(id+"F2.wireOp",EDGE,"E16.top"),sQuery(id+"F2.wireOp",EDGE,"E16.right")])]})});
            var Q64;
            Q64=makeQuery(id+"F3.boolean.opBoolean","COPY",EDGE,{"derivedFrom":makeQuery(id+"F3.opExtrude","CAP_EDGE",EDGE,{"disambiguationData":[OSD([sQuery(id+"F2.wireOp",EDGE,"E16.right")])],"isStart":false})});
            var Q65;
            Q65=makeQuery(id+"F3.boolean.opBoolean","COPY",EDGE,{"derivedFrom":makeQuery(id+"F3.opExtrude","SWEPT_EDGE",EDGE,{"disambiguationData":[OSD([sQuery(id+"F2.wireOp",EDGE,"E16.bottom"),sQuery(id+"F2.wireOp",EDGE,"E16.right")])]})});
            var Q66;
            {var subQ0=sQuery(id+"F2.wireOp",EDGE,"E18");var subQ1=sQuery(id+"F2.wireOp",EDGE,"E4");Q66=makeQuery(id+"F3.boolean.opBoolean","COPY",EDGE,{"derivedFrom":makeQuery(id+"F3.opExtrude","SWEPT_EDGE",EDGE,{"disambiguationData":[OSD([subQ1,subQ0]),TDD([makeQuery(id+"F2.imprint","INTERSECT",VERTEX,{"disambiguationData":[OD(0.0)],"derivedFrom":[subQ1,subQ0]})])]})});}
            var Q67;
            {var subQ0=sQuery(id+"F2.wireOp",EDGE,"E18");var subQ1=sQuery(id+"F2.wireOp",EDGE,"E4");Q67=makeQuery(id+"F3.boolean.opBoolean","COPY",EDGE,{"derivedFrom":makeQuery(id+"F3.opExtrude","SWEPT_EDGE",EDGE,{"disambiguationData":[OSD([subQ1,subQ0]),TDD([makeQuery(id+"F2.imprint","INTERSECT",VERTEX,{"disambiguationData":[OD(1.0)],"derivedFrom":[subQ1,subQ0]})])]})});}
            fillet(context, id + "F4", {"entities" : qUnion([Q0, Q1, Q2, Q3, Q4, Q5, Q6, Q7, Q8, Q9, Q10, Q11, Q12, Q13, Q14, Q15, Q16, Q17, Q18, Q19, Q20, Q21, Q22, Q23, Q24, Q25, Q26, Q27, Q28, Q29, Q30, Q31, Q32, Q33, Q34, Q35, Q36, Q37, Q38, Q39, Q40, Q41, Q42, Q43, Q44, Q45, Q46, Q47, Q48, Q49, Q50, Q51, Q52, Q53, Q54, Q55, Q56, Q57, Q58, Q59, Q60, Q61, Q62, Q63, Q64, Q65, Q66, Q67]), "radius" : 0.8 * mm, "tangentPropagation" : true, "allowEdgeOverflow" : false});
        }
        {
            var Q0;
            Q0=makeQuery(id+"F1.opExtrude","CAP_EDGE",EDGE,{"disambiguationData":[OSD([sQuery(id+"F0.wireOp",EDGE,"E0.right")])],"isStart":false});
            var Q1;
            Q1=makeQuery(id+"F1.opExtrude","CAP_EDGE",EDGE,{"disambiguationData":[OSD([sQuery(id+"F0.wireOp",EDGE,"E0.top")])],"isStart":false});
            var Q2;
            Q2=makeQuery(id+"F1.opExtrude","CAP_EDGE",EDGE,{"disambiguationData":[OSD([sQuery(id+"F0.wireOp",EDGE,"E0.bottom")])],"isStart":false});
            var Q3;
            Q3=makeQuery(id+"F1.opExtrude","CAP_EDGE",EDGE,{"disambiguationData":[OSD([sQuery(id+"F0.wireOp",EDGE,"E0.left")])],"isStart":false});
            var Q4;
            Q4=makeQuery(id+"F1.opExtrude","SWEPT_EDGE",EDGE,{"disambiguationData":[OSD([sQuery(id+"F0.wireOp",EDGE,"E0.top"),sQuery(id+"F0.wireOp",EDGE,"E0.right")])]});
            var Q5;
            Q5=makeQuery(id+"F1.opExtrude","SWEPT_EDGE",EDGE,{"disambiguationData":[OSD([sQuery(id+"F0.wireOp",EDGE,"E0.bottom"),sQuery(id+"F0.wireOp",EDGE,"E0.right")])]});
            var Q6;
            Q6=makeQuery(id+"F1.opExtrude","SWEPT_EDGE",EDGE,{"disambiguationData":[OSD([sQuery(id+"F0.wireOp",EDGE,"E0.bottom"),sQuery(id+"F0.wireOp",EDGE,"E0.left")])]});
            var Q7;
            Q7=makeQuery(id+"F1.opExtrude","SWEPT_EDGE",EDGE,{"disambiguationData":[OSD([sQuery(id+"F0.wireOp",EDGE,"E0.top"),sQuery(id+"F0.wireOp",EDGE,"E0.left")])]});
            fillet(context, id + "F5", {"entities" : qUnion([Q0, Q1, Q2, Q3, Q4, Q5, Q6, Q7]), "radius" : 3 * mm, "tangentPropagation" : true, "allowEdgeOverflow" : false});
        }
    });
